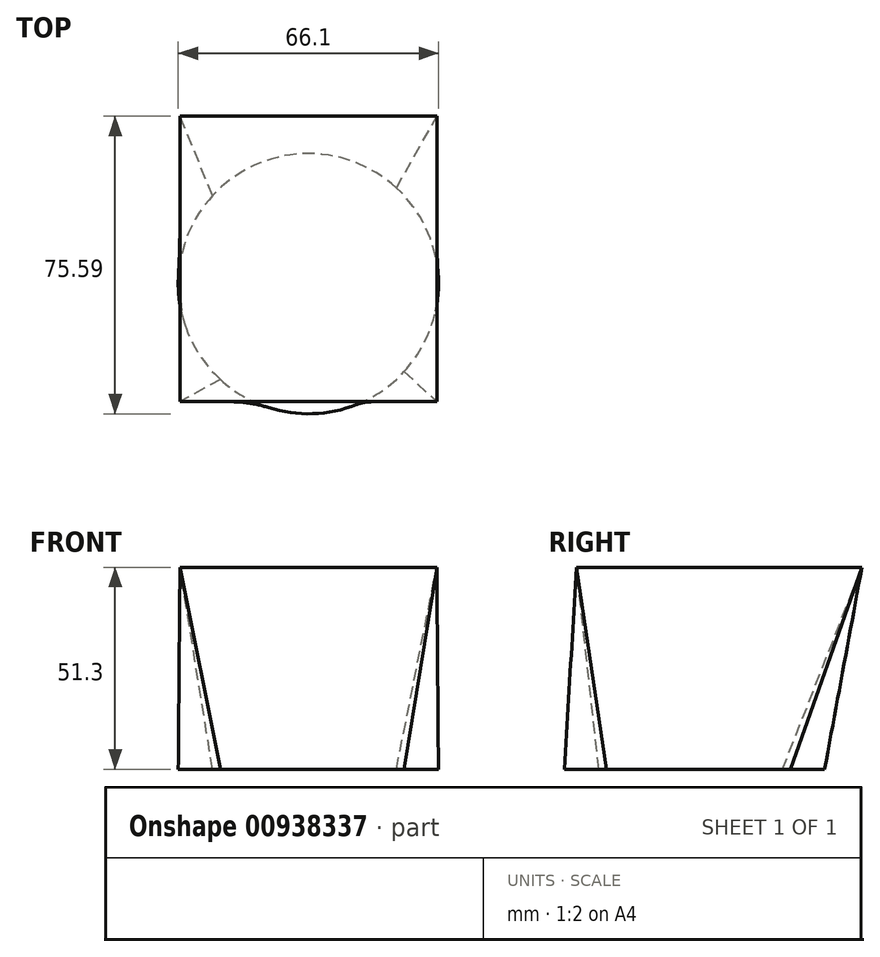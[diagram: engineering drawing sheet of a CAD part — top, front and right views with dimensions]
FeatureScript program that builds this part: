
annotation { "Feature Type Name" : "Feature", "Feature Type Description" : "" }
export const myFeature = defineFeature(function(context is Context, id is Id, definition is map)
    precondition{}
    {
        {
            var Q0;
            Q0=qCreatedBy(makeId("Top.planeOp"),FACE);
            cPlane(context, id + "F0", {"entities" : qUnion([Q0]), "cplaneType" : CPlaneType.OFFSET, "offset" : 51.3 * mm, "width" : 150 * mm, "height" : 150 * mm});
        }
        {
            var Q0;
            Q0=qCreatedBy(makeId("Top.planeOp"),FACE);
            var sketch = newSketch(context, id + "F1", { "sketchPlane" : qUnion([Q0])});
            skCircle(sketch, "E0", {"center": v(0, 0) * mm, "radius": 33.05 * mm});
            skSolve(sketch);
        }
        {
            var Q0;
            Q0=qCreatedBy(id+"F0.planeOp",FACE);
            var sketch = newSketch(context, id + "F2", { "sketchPlane" : qUnion([Q0])});
            skLineSegment(sketch, "E1.bottom", {"start": v(32.62, -29.98) * mm, "end": v(-32.62, -29.98) * mm});
            skLineSegment(sketch, "E1.top", {"start": v(32.62, 42.54) * mm, "end": v(-32.62, 42.54) * mm});
            skLineSegment(sketch, "E1.left", {"start": v(32.62, -29.98) * mm, "end": v(32.62, 42.54) * mm});
            skLineSegment(sketch, "E1.right", {"start": v(-32.62, -29.98) * mm, "end": v(-32.62, 42.54) * mm});
            skPoint(sketch, "E1.middle", {"position": v(0, 6.28) * mm});
            skSolve(sketch);
        }
        {
            var Q0;
            Q0=makeQuery(id+"F1.imprint","IMPRINT",FACE,{"disambiguationData":[TD([[makeQuery(id+"F1.imprint","IMPRINT",EDGE,{"derivedFrom":sQuery(id+"F1.wireOp",EDGE,"E0")}),1.0]])]});
            var Q1;
            Q1=makeQuery(id+"F2.imprint","IMPRINT",FACE,{"disambiguationData":[TD([[makeQuery(id+"F2.imprint","IMPRINT",EDGE,{"derivedFrom":sQuery(id+"F2.wireOp",EDGE,"E1.bottom")}),-1.0]])]});
            loft(context, id + "F3", {"sheetProfilesArray" : [{ "sheetProfileEntities" : qUnion([Q0]) }, { "sheetProfileEntities" : qUnion([Q1]) }]});
        }
    });
